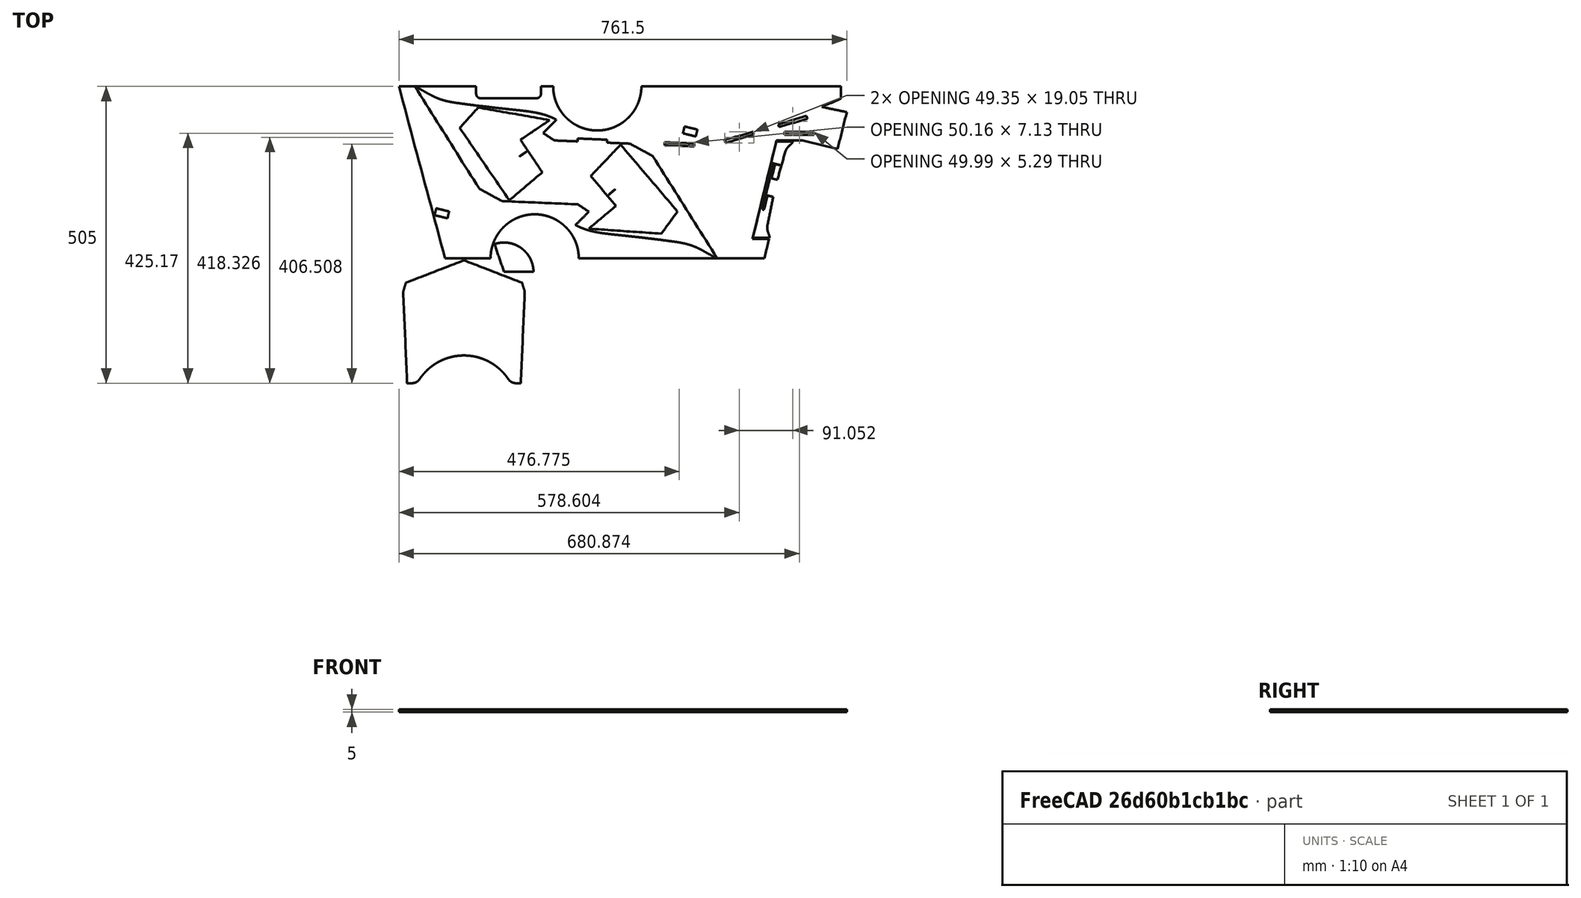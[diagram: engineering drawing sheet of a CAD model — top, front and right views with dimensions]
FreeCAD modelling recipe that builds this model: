
FCSTD DOCUMENT  (FreeCAD 0.19R)
Label: F-35 Page 2
License: All rights reserved
LicenseURL: http://en.wikipedia.org/wiki/All_rights_reserved
objects: Sketcher::SketchObject×7, PartDesign::Pad×7, PartDesign::Body×7
note: 28 computed .brp shape members not serialized (recipe doc carries the construction recipe); baked Part::Feature solids carry a one-line shape summary decoded from their .brp

FEATURE [Sketcher::SketchObject] Sketch
  FullyConstrained = false
  sketch-geometry (125):
    g0: BSplineCurve PolesCount=2 KnotsCount=2 Degree=1 IsPeriodic=0
    g1: BSplineCurve PolesCount=2 KnotsCount=2 Degree=1 IsPeriodic=0
    g2: BSplineCurve PolesCount=2 KnotsCount=2 Degree=1 IsPeriodic=0
    g3: BSplineCurve PolesCount=2 KnotsCount=2 Degree=1 IsPeriodic=0
    g4: BSplineCurve PolesCount=2 KnotsCount=2 Degree=1 IsPeriodic=0
    g5: BSplineCurve PolesCount=2 KnotsCount=2 Degree=1 IsPeriodic=0
    g6: BSplineCurve PolesCount=2 KnotsCount=2 Degree=1 IsPeriodic=0
    g7: BSplineCurve PolesCount=2 KnotsCount=2 Degree=1 IsPeriodic=0
    g8: BSplineCurve PolesCount=2 KnotsCount=2 Degree=1 IsPeriodic=0
    g9: BSplineCurve PolesCount=2 KnotsCount=2 Degree=1 IsPeriodic=0
    g10: BSplineCurve PolesCount=2 KnotsCount=2 Degree=1 IsPeriodic=0
    g11: BSplineCurve PolesCount=2 KnotsCount=2 Degree=1 IsPeriodic=0
    g12: BSplineCurve PolesCount=2 KnotsCount=2 Degree=1 IsPeriodic=0
    g13: BSplineCurve PolesCount=2 KnotsCount=2 Degree=1 IsPeriodic=0
    g14: BSplineCurve PolesCount=2 KnotsCount=2 Degree=1 IsPeriodic=0
    g15: BSplineCurve PolesCount=2 KnotsCount=2 Degree=1 IsPeriodic=0
    g16: BSplineCurve PolesCount=2 KnotsCount=2 Degree=1 IsPeriodic=0
    g17: BSplineCurve PolesCount=2 KnotsCount=2 Degree=1 IsPeriodic=0
    g18: BSplineCurve PolesCount=2 KnotsCount=2 Degree=1 IsPeriodic=0
    g19: BSplineCurve PolesCount=2 KnotsCount=2 Degree=1 IsPeriodic=0
    g20: BSplineCurve PolesCount=2 KnotsCount=2 Degree=1 IsPeriodic=0
    g21: BSplineCurve PolesCount=2 KnotsCount=2 Degree=1 IsPeriodic=0
    g22: BSplineCurve PolesCount=2 KnotsCount=2 Degree=1 IsPeriodic=0
    g23: BSplineCurve PolesCount=2 KnotsCount=2 Degree=1 IsPeriodic=0
    g24: BSplineCurve PolesCount=2 KnotsCount=2 Degree=1 IsPeriodic=0
    g25: BSplineCurve PolesCount=2 KnotsCount=2 Degree=1 IsPeriodic=0
    g26: BSplineCurve PolesCount=2 KnotsCount=2 Degree=1 IsPeriodic=0
    g27: BSplineCurve PolesCount=2 KnotsCount=2 Degree=1 IsPeriodic=0
    g28: BSplineCurve PolesCount=2 KnotsCount=2 Degree=1 IsPeriodic=0
    g29: BSplineCurve PolesCount=2 KnotsCount=2 Degree=1 IsPeriodic=0
    g30: BSplineCurve PolesCount=2 KnotsCount=2 Degree=1 IsPeriodic=0
    g31: BSplineCurve PolesCount=2 KnotsCount=2 Degree=1 IsPeriodic=0
    g32: BSplineCurve PolesCount=2 KnotsCount=2 Degree=1 IsPeriodic=0
    g33: BSplineCurve PolesCount=2 KnotsCount=2 Degree=1 IsPeriodic=0
    g34: BSplineCurve PolesCount=2 KnotsCount=2 Degree=1 IsPeriodic=0
    g35: BSplineCurve PolesCount=2 KnotsCount=2 Degree=1 IsPeriodic=0
    g36: BSplineCurve PolesCount=2 KnotsCount=2 Degree=1 IsPeriodic=0
    g37: BSplineCurve PolesCount=2 KnotsCount=2 Degree=1 IsPeriodic=0
    g38: BSplineCurve PolesCount=2 KnotsCount=2 Degree=1 IsPeriodic=0
    g39: BSplineCurve PolesCount=2 KnotsCount=2 Degree=1 IsPeriodic=0
    g40: BSplineCurve PolesCount=2 KnotsCount=2 Degree=1 IsPeriodic=0
    g41: BSplineCurve PolesCount=2 KnotsCount=2 Degree=1 IsPeriodic=0
    g42: BSplineCurve PolesCount=2 KnotsCount=2 Degree=1 IsPeriodic=0
    g43: BSplineCurve PolesCount=2 KnotsCount=2 Degree=1 IsPeriodic=0
    g44: BSplineCurve PolesCount=2 KnotsCount=2 Degree=1 IsPeriodic=0
    g45: BSplineCurve PolesCount=2 KnotsCount=2 Degree=1 IsPeriodic=0
    g46: BSplineCurve PolesCount=2 KnotsCount=2 Degree=1 IsPeriodic=0
    g47: BSplineCurve PolesCount=2 KnotsCount=2 Degree=1 IsPeriodic=0
    g48: BSplineCurve PolesCount=2 KnotsCount=2 Degree=1 IsPeriodic=0
    g49: BSplineCurve PolesCount=2 KnotsCount=2 Degree=1 IsPeriodic=0
    g50: BSplineCurve PolesCount=2 KnotsCount=2 Degree=1 IsPeriodic=0
    g51: BSplineCurve PolesCount=2 KnotsCount=2 Degree=1 IsPeriodic=0
    g52: BSplineCurve PolesCount=2 KnotsCount=2 Degree=1 IsPeriodic=0
    g53: BSplineCurve PolesCount=2 KnotsCount=2 Degree=1 IsPeriodic=0
    g54: BSplineCurve PolesCount=2 KnotsCount=2 Degree=1 IsPeriodic=0
    g55: BSplineCurve PolesCount=2 KnotsCount=2 Degree=1 IsPeriodic=0
    g56: BSplineCurve PolesCount=2 KnotsCount=2 Degree=1 IsPeriodic=0
    g57: BSplineCurve PolesCount=2 KnotsCount=2 Degree=1 IsPeriodic=0
    g58: BSplineCurve PolesCount=2 KnotsCount=2 Degree=1 IsPeriodic=0
    g59: BSplineCurve PolesCount=2 KnotsCount=2 Degree=1 IsPeriodic=0
    g60: BSplineCurve PolesCount=2 KnotsCount=2 Degree=1 IsPeriodic=0
    g61: BSplineCurve PolesCount=2 KnotsCount=2 Degree=1 IsPeriodic=0
    g62: BSplineCurve PolesCount=2 KnotsCount=2 Degree=1 IsPeriodic=0
    g63: BSplineCurve PolesCount=2 KnotsCount=2 Degree=1 IsPeriodic=0
    g64: BSplineCurve PolesCount=2 KnotsCount=2 Degree=1 IsPeriodic=0
    g65: BSplineCurve PolesCount=2 KnotsCount=2 Degree=1 IsPeriodic=0
    g66: BSplineCurve PolesCount=2 KnotsCount=2 Degree=1 IsPeriodic=0
    g67: BSplineCurve PolesCount=2 KnotsCount=2 Degree=1 IsPeriodic=0
    g68: BSplineCurve PolesCount=2 KnotsCount=2 Degree=1 IsPeriodic=0
    g69: BSplineCurve PolesCount=2 KnotsCount=2 Degree=1 IsPeriodic=0
    g70: BSplineCurve PolesCount=2 KnotsCount=2 Degree=1 IsPeriodic=0
    g71: BSplineCurve PolesCount=2 KnotsCount=2 Degree=1 IsPeriodic=0
    g72: BSplineCurve PolesCount=2 KnotsCount=2 Degree=1 IsPeriodic=0
    g73: BSplineCurve PolesCount=2 KnotsCount=2 Degree=1 IsPeriodic=0
    g74: BSplineCurve PolesCount=2 KnotsCount=2 Degree=1 IsPeriodic=0
    g75: BSplineCurve PolesCount=2 KnotsCount=2 Degree=1 IsPeriodic=0
    g76: BSplineCurve PolesCount=2 KnotsCount=2 Degree=1 IsPeriodic=0
    g77: BSplineCurve PolesCount=2 KnotsCount=2 Degree=1 IsPeriodic=0
    g78: BSplineCurve PolesCount=2 KnotsCount=2 Degree=1 IsPeriodic=0
    g79: BSplineCurve PolesCount=2 KnotsCount=2 Degree=1 IsPeriodic=0
    g80: BSplineCurve PolesCount=2 KnotsCount=2 Degree=1 IsPeriodic=0
    g81: BSplineCurve PolesCount=2 KnotsCount=2 Degree=1 IsPeriodic=0
    g82: BSplineCurve PolesCount=2 KnotsCount=2 Degree=1 IsPeriodic=0
    g83: BSplineCurve PolesCount=2 KnotsCount=2 Degree=1 IsPeriodic=0
    g84: BSplineCurve PolesCount=2 KnotsCount=2 Degree=1 IsPeriodic=0
    g85: BSplineCurve PolesCount=2 KnotsCount=2 Degree=1 IsPeriodic=0
    g86: BSplineCurve PolesCount=2 KnotsCount=2 Degree=1 IsPeriodic=0
    g87: BSplineCurve PolesCount=2 KnotsCount=2 Degree=1 IsPeriodic=0
    g88: BSplineCurve PolesCount=2 KnotsCount=2 Degree=1 IsPeriodic=0
    g89: BSplineCurve PolesCount=2 KnotsCount=2 Degree=1 IsPeriodic=0
    g90: BSplineCurve PolesCount=2 KnotsCount=2 Degree=1 IsPeriodic=0
    g91: BSplineCurve PolesCount=2 KnotsCount=2 Degree=1 IsPeriodic=0
    g92: BSplineCurve PolesCount=2 KnotsCount=2 Degree=1 IsPeriodic=0
    g93: BSplineCurve PolesCount=2 KnotsCount=2 Degree=1 IsPeriodic=0
    g94: BSplineCurve PolesCount=2 KnotsCount=2 Degree=1 IsPeriodic=0
    g95: BSplineCurve PolesCount=2 KnotsCount=2 Degree=1 IsPeriodic=0
    g96: BSplineCurve PolesCount=2 KnotsCount=2 Degree=1 IsPeriodic=0
    g97: BSplineCurve PolesCount=2 KnotsCount=2 Degree=1 IsPeriodic=0
    g98: BSplineCurve PolesCount=2 KnotsCount=2 Degree=1 IsPeriodic=0
    g99: BSplineCurve PolesCount=2 KnotsCount=2 Degree=1 IsPeriodic=0
    g100: BSplineCurve PolesCount=2 KnotsCount=2 Degree=1 IsPeriodic=0
    g101: BSplineCurve PolesCount=2 KnotsCount=2 Degree=1 IsPeriodic=0
    g102: BSplineCurve PolesCount=2 KnotsCount=2 Degree=1 IsPeriodic=0
    g103: BSplineCurve PolesCount=2 KnotsCount=2 Degree=1 IsPeriodic=0
    g104: BSplineCurve PolesCount=2 KnotsCount=2 Degree=1 IsPeriodic=0
    g105: BSplineCurve PolesCount=2 KnotsCount=2 Degree=1 IsPeriodic=0
    g106: BSplineCurve PolesCount=2 KnotsCount=2 Degree=1 IsPeriodic=0
    g107: BSplineCurve PolesCount=2 KnotsCount=2 Degree=1 IsPeriodic=0
    g108: BSplineCurve PolesCount=2 KnotsCount=2 Degree=1 IsPeriodic=0
    g109: BSplineCurve PolesCount=2 KnotsCount=2 Degree=1 IsPeriodic=0
    g110: BSplineCurve PolesCount=2 KnotsCount=2 Degree=1 IsPeriodic=0
    g111: BSplineCurve PolesCount=2 KnotsCount=2 Degree=1 IsPeriodic=0
    g112: BSplineCurve PolesCount=2 KnotsCount=2 Degree=1 IsPeriodic=0
    g113: BSplineCurve PolesCount=2 KnotsCount=2 Degree=1 IsPeriodic=0
    g114: BSplineCurve PolesCount=2 KnotsCount=2 Degree=1 IsPeriodic=0
    g115: BSplineCurve PolesCount=2 KnotsCount=2 Degree=1 IsPeriodic=0
    g116: BSplineCurve PolesCount=2 KnotsCount=2 Degree=1 IsPeriodic=0
    g117: BSplineCurve PolesCount=2 KnotsCount=2 Degree=1 IsPeriodic=0
    g118: BSplineCurve PolesCount=2 KnotsCount=2 Degree=1 IsPeriodic=0
    g119: BSplineCurve PolesCount=2 KnotsCount=2 Degree=1 IsPeriodic=0
    g120: BSplineCurve PolesCount=2 KnotsCount=2 Degree=1 IsPeriodic=0
    g121: BSplineCurve PolesCount=2 KnotsCount=2 Degree=1 IsPeriodic=0
    g122: BSplineCurve PolesCount=2 KnotsCount=2 Degree=1 IsPeriodic=0
    g123: BSplineCurve PolesCount=2 KnotsCount=2 Degree=1 IsPeriodic=0
    g124: BSplineCurve PolesCount=2 KnotsCount=2 Degree=1 IsPeriodic=0
  constraints (76):
    c: Coincident(g20,g21)
    c: Coincident(g21,g22)
    c: Coincident(g22,g23)
    c: Coincident(g23,g24)
    c: Coincident(g24,g25)
    c: Coincident(g25,g26)
    c: Coincident(g26,g27)
    c: Coincident(g29,g30)
    c: Coincident(g30,g31)
    c: Coincident(g31,g32)
    c: Coincident(g32,g33)
    c: Coincident(g33,g34)
    c: Coincident(g34,g35)
    c: Coincident(g35,g36)
    c: Coincident(g39,g40)
    c: Coincident(g40,g41)
    c: Coincident(g41,g42)
    c: Coincident(g42,g43)
    c: Coincident(g43,g44)
    c: Coincident(g44,g45)
    c: Coincident(g45,g46)
    c: Coincident(g46,g47)
    c: Coincident(g47,g48)
    c: Coincident(g48,g49)
    c: Coincident(g49,g50)
    c: Coincident(g50,g51)
    c: Coincident(g51,g52)
    c: Coincident(g52,g53)
    c: Coincident(g53,g54)
    c: Coincident(g54,g55)
    c: Coincident(g55,g56)
    c: Coincident(g56,g57)
    c: Coincident(g57,g58)
    c: Coincident(g58,g59)
    c: Coincident(g59,g60)
    c: Coincident(g60,g61)
    c: Coincident(g61,g62)
    c: Coincident(g62,g63)
    c: Coincident(g63,g64)
    c: Coincident(g64,g65)
    c: Coincident(g65,g66)
    c: Coincident(g66,g67)
    c: Coincident(g67,g68)
    c: Coincident(g68,g69)
    c: Coincident(g69,g70)
    c: Coincident(g70,g71)
    c: Coincident(g71,g72)
    c: Coincident(g72,g73)
    c: Coincident(g73,g74)
    c: Coincident(g74,g75)
    c: Coincident(g75,g76)
    c: Coincident(g76,g77)
    c: Coincident(g77,g78)
    c: Coincident(g78,g79)
    c: Coincident(g79,g80)
    c: Coincident(g80,g81)
    c: Coincident(g81,g82)
    c: Coincident(g82,g83)
    c: Coincident(g103,g104)
    c: Coincident(g104,g105)
    c: Coincident(g105,g106)
    c: Coincident(g106,g107)
    c: Coincident(g107,g108)
    c: Coincident(g108,g109)
    c: Coincident(g109,g110)
    c: Coincident(g110,g111)
    c: Coincident(g111,g112)
    c: Coincident(g112,g113)
    c: Coincident(g113,g114)
    c: Coincident(g114,g115)
    c: Coincident(g115,g116)
    c: Coincident(g116,g117)
    c: Coincident(g117,g118)
    c: Coincident(g118,g119)
    c: Coincident(g119,g120)
    c: Coincident(g120,g121)
FEATURE [Sketcher::SketchObject] Sketch001
  FullyConstrained = false
  sketch-geometry (36):
    g0: BSplineCurve PolesCount=2 KnotsCount=2 Degree=1 IsPeriodic=0
    g1: BSplineCurve PolesCount=2 KnotsCount=2 Degree=1 IsPeriodic=0
    g2: BSplineCurve PolesCount=2 KnotsCount=2 Degree=1 IsPeriodic=0
    g3: BSplineCurve PolesCount=2 KnotsCount=2 Degree=1 IsPeriodic=0
    g4: BSplineCurve PolesCount=2 KnotsCount=2 Degree=1 IsPeriodic=0
    g5: BSplineCurve PolesCount=2 KnotsCount=2 Degree=1 IsPeriodic=0
    g6: BSplineCurve PolesCount=2 KnotsCount=2 Degree=1 IsPeriodic=0
    g7: BSplineCurve PolesCount=2 KnotsCount=2 Degree=1 IsPeriodic=0
    g8: BSplineCurve PolesCount=2 KnotsCount=2 Degree=1 IsPeriodic=0
    g9: BSplineCurve PolesCount=2 KnotsCount=2 Degree=1 IsPeriodic=0
    g10: BSplineCurve PolesCount=2 KnotsCount=2 Degree=1 IsPeriodic=0
    g11: BSplineCurve PolesCount=2 KnotsCount=2 Degree=1 IsPeriodic=0
    g12: BSplineCurve PolesCount=2 KnotsCount=2 Degree=1 IsPeriodic=0
    g13: BSplineCurve PolesCount=2 KnotsCount=2 Degree=1 IsPeriodic=0
    g14: BSplineCurve PolesCount=2 KnotsCount=2 Degree=1 IsPeriodic=0
    g15: BSplineCurve PolesCount=2 KnotsCount=2 Degree=1 IsPeriodic=0
    g16: BSplineCurve PolesCount=2 KnotsCount=2 Degree=1 IsPeriodic=0
    g17: BSplineCurve PolesCount=2 KnotsCount=2 Degree=1 IsPeriodic=0
    g18: BSplineCurve PolesCount=2 KnotsCount=2 Degree=1 IsPeriodic=0
    g19: BSplineCurve PolesCount=2 KnotsCount=2 Degree=1 IsPeriodic=0
    g20: BSplineCurve PolesCount=2 KnotsCount=2 Degree=1 IsPeriodic=0
    g21: BSplineCurve PolesCount=2 KnotsCount=2 Degree=1 IsPeriodic=0
    g22: BSplineCurve PolesCount=2 KnotsCount=2 Degree=1 IsPeriodic=0
    g23: BSplineCurve PolesCount=2 KnotsCount=2 Degree=1 IsPeriodic=0
    g24: BSplineCurve PolesCount=2 KnotsCount=2 Degree=1 IsPeriodic=0
    g25: BSplineCurve PolesCount=2 KnotsCount=2 Degree=1 IsPeriodic=0
    g26: BSplineCurve PolesCount=2 KnotsCount=2 Degree=1 IsPeriodic=0
    g27: BSplineCurve PolesCount=2 KnotsCount=2 Degree=1 IsPeriodic=0
    g28: BSplineCurve PolesCount=2 KnotsCount=2 Degree=1 IsPeriodic=0
    g29: BSplineCurve PolesCount=2 KnotsCount=2 Degree=1 IsPeriodic=0
    g30: BSplineCurve PolesCount=2 KnotsCount=2 Degree=1 IsPeriodic=0
    g31: BSplineCurve PolesCount=2 KnotsCount=2 Degree=1 IsPeriodic=0
    g32: BSplineCurve PolesCount=2 KnotsCount=2 Degree=1 IsPeriodic=0
    g33: BSplineCurve PolesCount=2 KnotsCount=2 Degree=1 IsPeriodic=0
    g34: BSplineCurve PolesCount=2 KnotsCount=2 Degree=1 IsPeriodic=0
    g35: LineSegment StartX=748.511 StartY=-199.265 StartZ=0 EndX=708.789 EndY=-363.131 EndZ=0
  constraints (16):
    c: Coincident(g11,g12)
    c: Coincident(g12,g13)
    c: Coincident(g13,g14)
    c: Coincident(g14,g15)
    c: Coincident(g15,g16)
    c: Coincident(g16,g17)
    c: Coincident(g17,g18)
    c: Coincident(g27,g28)
    c: Coincident(g28,g29)
    c: Coincident(g29,g30)
    c: Coincident(g30,g31)
    c: Coincident(g31,g32)
    c: Coincident(g32,g33)
    c: Coincident(g33,g34)
    c: Coincident(g7,g35)
    c: Coincident(g8,g35)
FEATURE [Sketcher::SketchObject] Sketch002
  FullyConstrained = false
  sketch-geometry (77):
    g0: BSplineCurve PolesCount=2 KnotsCount=2 Degree=1 IsPeriodic=0
    g1: BSplineCurve PolesCount=2 KnotsCount=2 Degree=1 IsPeriodic=0
    g2: BSplineCurve PolesCount=2 KnotsCount=2 Degree=1 IsPeriodic=0
    g3: BSplineCurve PolesCount=2 KnotsCount=2 Degree=1 IsPeriodic=0
    g4: BSplineCurve PolesCount=2 KnotsCount=2 Degree=1 IsPeriodic=0
    g5: BSplineCurve PolesCount=2 KnotsCount=2 Degree=1 IsPeriodic=0
    g6: BSplineCurve PolesCount=2 KnotsCount=2 Degree=1 IsPeriodic=0
    g7: BSplineCurve PolesCount=2 KnotsCount=2 Degree=1 IsPeriodic=0
    g8: BSplineCurve PolesCount=2 KnotsCount=2 Degree=1 IsPeriodic=0
    g9: BSplineCurve PolesCount=2 KnotsCount=2 Degree=1 IsPeriodic=0
    g10: BSplineCurve PolesCount=2 KnotsCount=2 Degree=1 IsPeriodic=0
    g11: BSplineCurve PolesCount=2 KnotsCount=2 Degree=1 IsPeriodic=0
    g12: BSplineCurve PolesCount=2 KnotsCount=2 Degree=1 IsPeriodic=0
    g13: BSplineCurve PolesCount=2 KnotsCount=2 Degree=1 IsPeriodic=0
    g14: BSplineCurve PolesCount=2 KnotsCount=2 Degree=1 IsPeriodic=0
    g15: BSplineCurve PolesCount=2 KnotsCount=2 Degree=1 IsPeriodic=0
    g16: BSplineCurve PolesCount=2 KnotsCount=2 Degree=1 IsPeriodic=0
    g17: BSplineCurve PolesCount=2 KnotsCount=2 Degree=1 IsPeriodic=0
    g18: BSplineCurve PolesCount=2 KnotsCount=2 Degree=1 IsPeriodic=0
    g19: BSplineCurve PolesCount=2 KnotsCount=2 Degree=1 IsPeriodic=0
    g20: BSplineCurve PolesCount=2 KnotsCount=2 Degree=1 IsPeriodic=0
    g21: BSplineCurve PolesCount=2 KnotsCount=2 Degree=1 IsPeriodic=0
    g22: BSplineCurve PolesCount=2 KnotsCount=2 Degree=1 IsPeriodic=0
    g23: BSplineCurve PolesCount=2 KnotsCount=2 Degree=1 IsPeriodic=0
    g24: BSplineCurve PolesCount=2 KnotsCount=2 Degree=1 IsPeriodic=0
    g25: BSplineCurve PolesCount=2 KnotsCount=2 Degree=1 IsPeriodic=0
    g26: BSplineCurve PolesCount=2 KnotsCount=2 Degree=1 IsPeriodic=0
    g27: BSplineCurve PolesCount=2 KnotsCount=2 Degree=1 IsPeriodic=0
    g28: BSplineCurve PolesCount=2 KnotsCount=2 Degree=1 IsPeriodic=0
    g29: BSplineCurve PolesCount=2 KnotsCount=2 Degree=1 IsPeriodic=0
    g30: BSplineCurve PolesCount=2 KnotsCount=2 Degree=1 IsPeriodic=0
    g31: BSplineCurve PolesCount=2 KnotsCount=2 Degree=1 IsPeriodic=0
    g32: BSplineCurve PolesCount=2 KnotsCount=2 Degree=1 IsPeriodic=0
    g33: BSplineCurve PolesCount=2 KnotsCount=2 Degree=1 IsPeriodic=0
    g34: BSplineCurve PolesCount=2 KnotsCount=2 Degree=1 IsPeriodic=0
    g35: BSplineCurve PolesCount=2 KnotsCount=2 Degree=1 IsPeriodic=0
    g36: BSplineCurve PolesCount=2 KnotsCount=2 Degree=1 IsPeriodic=0
    g37: BSplineCurve PolesCount=2 KnotsCount=2 Degree=1 IsPeriodic=0
    g38: BSplineCurve PolesCount=2 KnotsCount=2 Degree=1 IsPeriodic=0
    g39: BSplineCurve PolesCount=2 KnotsCount=2 Degree=1 IsPeriodic=0
    g40: BSplineCurve PolesCount=2 KnotsCount=2 Degree=1 IsPeriodic=0
    g41: BSplineCurve PolesCount=2 KnotsCount=2 Degree=1 IsPeriodic=0
    g42: BSplineCurve PolesCount=2 KnotsCount=2 Degree=1 IsPeriodic=0
    g43: BSplineCurve PolesCount=2 KnotsCount=2 Degree=1 IsPeriodic=0
    g44: BSplineCurve PolesCount=2 KnotsCount=2 Degree=1 IsPeriodic=0
    g45: BSplineCurve PolesCount=2 KnotsCount=2 Degree=1 IsPeriodic=0
    g46: BSplineCurve PolesCount=2 KnotsCount=2 Degree=1 IsPeriodic=0
    g47: BSplineCurve PolesCount=2 KnotsCount=2 Degree=1 IsPeriodic=0
    g48: BSplineCurve PolesCount=2 KnotsCount=2 Degree=1 IsPeriodic=0
    g49: BSplineCurve PolesCount=2 KnotsCount=2 Degree=1 IsPeriodic=0
    g50: BSplineCurve PolesCount=2 KnotsCount=2 Degree=1 IsPeriodic=0
    g51: BSplineCurve PolesCount=2 KnotsCount=2 Degree=1 IsPeriodic=0
    g52: BSplineCurve PolesCount=2 KnotsCount=2 Degree=1 IsPeriodic=0
    g53: BSplineCurve PolesCount=2 KnotsCount=2 Degree=1 IsPeriodic=0
    g54: BSplineCurve PolesCount=2 KnotsCount=2 Degree=1 IsPeriodic=0
    g55: BSplineCurve PolesCount=2 KnotsCount=2 Degree=1 IsPeriodic=0
    g56: BSplineCurve PolesCount=2 KnotsCount=2 Degree=1 IsPeriodic=0
    g57: BSplineCurve PolesCount=2 KnotsCount=2 Degree=1 IsPeriodic=0
    g58: BSplineCurve PolesCount=2 KnotsCount=2 Degree=1 IsPeriodic=0
    g59: BSplineCurve PolesCount=2 KnotsCount=2 Degree=1 IsPeriodic=0
    g60: BSplineCurve PolesCount=2 KnotsCount=2 Degree=1 IsPeriodic=0
    g61: BSplineCurve PolesCount=2 KnotsCount=2 Degree=1 IsPeriodic=0
    g62: BSplineCurve PolesCount=2 KnotsCount=2 Degree=1 IsPeriodic=0
    g63: BSplineCurve PolesCount=2 KnotsCount=2 Degree=1 IsPeriodic=0
    g64: BSplineCurve PolesCount=2 KnotsCount=2 Degree=1 IsPeriodic=0
    g65: BSplineCurve PolesCount=2 KnotsCount=2 Degree=1 IsPeriodic=0
    g66: BSplineCurve PolesCount=2 KnotsCount=2 Degree=1 IsPeriodic=0
    g67: BSplineCurve PolesCount=2 KnotsCount=2 Degree=1 IsPeriodic=0
    g68: BSplineCurve PolesCount=2 KnotsCount=2 Degree=1 IsPeriodic=0
    g69: BSplineCurve PolesCount=2 KnotsCount=2 Degree=1 IsPeriodic=0
    g70: BSplineCurve PolesCount=2 KnotsCount=2 Degree=1 IsPeriodic=0
    g71: BSplineCurve PolesCount=2 KnotsCount=2 Degree=1 IsPeriodic=0
    g72: BSplineCurve PolesCount=2 KnotsCount=2 Degree=1 IsPeriodic=0
    g73: BSplineCurve PolesCount=2 KnotsCount=2 Degree=1 IsPeriodic=0
    g74: BSplineCurve PolesCount=2 KnotsCount=2 Degree=1 IsPeriodic=0
    g75: BSplineCurve PolesCount=2 KnotsCount=2 Degree=1 IsPeriodic=0
    g76: BSplineCurve PolesCount=2 KnotsCount=2 Degree=1 IsPeriodic=0
  constraints (62):
    c: Coincident(g6,g7)
    c: Coincident(g7,g8)
    c: Coincident(g8,g9)
    c: Coincident(g9,g10)
    c: Coincident(g10,g11)
    c: Coincident(g11,g12)
    c: Coincident(g12,g13)
    c: Coincident(g13,g14)
    c: Coincident(g14,g15)
    c: Coincident(g15,g16)
    c: Coincident(g16,g17)
    c: Coincident(g17,g18)
    c: Coincident(g18,g19)
    c: Coincident(g19,g20)
    c: Coincident(g20,g21)
    c: Coincident(g21,g22)
    c: Coincident(g22,g23)
    c: Coincident(g23,g24)
    c: Coincident(g25,g26)
    c: Coincident(g26,g27)
    c: Coincident(g27,g28)
    c: Coincident(g28,g29)
    c: Coincident(g29,g30)
    c: Coincident(g30,g31)
    c: Coincident(g31,g32)
    c: Coincident(g32,g33)
    c: Coincident(g33,g34)
    c: Coincident(g34,g35)
    c: Coincident(g35,g36)
    c: Coincident(g36,g37)
    c: Coincident(g37,g38)
    c: Coincident(g38,g39)
    c: Coincident(g39,g40)
    c: Coincident(g40,g41)
    c: Coincident(g41,g42)
    c: Coincident(g42,g43)
    c: Coincident(g43,g44)
    c: Coincident(g44,g45)
    c: Coincident(g45,g46)
    c: Coincident(g46,g47)
    c: Coincident(g47,g48)
    c: Coincident(g48,g49)
    c: Coincident(g49,g50)
    c: Coincident(g50,g51)
    c: Coincident(g51,g52)
    c: Coincident(g52,g53)
    c: Coincident(g53,g54)
    c: Coincident(g54,g55)
    c: Coincident(g55,g56)
    c: Coincident(g56,g57)
    c: Coincident(g57,g58)
    c: Coincident(g58,g59)
    c: Coincident(g59,g60)
    c: Coincident(g60,g61)
    c: Coincident(g61,g62)
    c: Coincident(g62,g63)
    c: Coincident(g63,g64)
    c: Coincident(g64,g65)
    c: Coincident(g65,g66)
    c: Coincident(g66,g67)
    c: Coincident(g67,g68)
    c: Coincident(g68,g69)
FEATURE [Sketcher::SketchObject] Sketch003
  FullyConstrained = false
  sketch-geometry (10):
    g0: BSplineCurve PolesCount=2 KnotsCount=2 Degree=1 IsPeriodic=0
    g1: BSplineCurve PolesCount=2 KnotsCount=2 Degree=1 IsPeriodic=0
    g2: BSplineCurve PolesCount=2 KnotsCount=2 Degree=1 IsPeriodic=0
    g3: BSplineCurve PolesCount=2 KnotsCount=2 Degree=1 IsPeriodic=0
    g4: BSplineCurve PolesCount=2 KnotsCount=2 Degree=1 IsPeriodic=0
    g5: BSplineCurve PolesCount=2 KnotsCount=2 Degree=1 IsPeriodic=0
    g6: BSplineCurve PolesCount=2 KnotsCount=2 Degree=1 IsPeriodic=0
    g7: BSplineCurve PolesCount=2 KnotsCount=2 Degree=1 IsPeriodic=0
    g8: BSplineCurve PolesCount=2 KnotsCount=2 Degree=1 IsPeriodic=0
    g9: BSplineCurve PolesCount=2 KnotsCount=2 Degree=1 IsPeriodic=0
FEATURE [Sketcher::SketchObject] Sketch004
  FullyConstrained = false
  sketch-geometry (10):
    g0: BSplineCurve PolesCount=2 KnotsCount=2 Degree=1 IsPeriodic=0
    g1: BSplineCurve PolesCount=2 KnotsCount=2 Degree=1 IsPeriodic=0
    g2: BSplineCurve PolesCount=2 KnotsCount=2 Degree=1 IsPeriodic=0
    g3: BSplineCurve PolesCount=2 KnotsCount=2 Degree=1 IsPeriodic=0
    g4: BSplineCurve PolesCount=2 KnotsCount=2 Degree=1 IsPeriodic=0
    g5: BSplineCurve PolesCount=2 KnotsCount=2 Degree=1 IsPeriodic=0
    g6: BSplineCurve PolesCount=2 KnotsCount=2 Degree=1 IsPeriodic=0
    g7: BSplineCurve PolesCount=2 KnotsCount=2 Degree=1 IsPeriodic=0
    g8: BSplineCurve PolesCount=2 KnotsCount=2 Degree=1 IsPeriodic=0
    g9: BSplineCurve PolesCount=2 KnotsCount=2 Degree=1 IsPeriodic=0
FEATURE [Sketcher::SketchObject] Sketch005
  FullyConstrained = false
  sketch-geometry (65):
    g0: BSplineCurve PolesCount=2 KnotsCount=2 Degree=1 IsPeriodic=0
    g1: BSplineCurve PolesCount=2 KnotsCount=2 Degree=1 IsPeriodic=0
    g2: BSplineCurve PolesCount=2 KnotsCount=2 Degree=1 IsPeriodic=0
    g3: BSplineCurve PolesCount=2 KnotsCount=2 Degree=1 IsPeriodic=0
    g4: BSplineCurve PolesCount=2 KnotsCount=2 Degree=1 IsPeriodic=0
    g5: BSplineCurve PolesCount=2 KnotsCount=2 Degree=1 IsPeriodic=0
    g6: BSplineCurve PolesCount=2 KnotsCount=2 Degree=1 IsPeriodic=0
    g7: BSplineCurve PolesCount=2 KnotsCount=2 Degree=1 IsPeriodic=0
    g8: BSplineCurve PolesCount=2 KnotsCount=2 Degree=1 IsPeriodic=0
    g9: BSplineCurve PolesCount=2 KnotsCount=2 Degree=1 IsPeriodic=0
    g10: BSplineCurve PolesCount=2 KnotsCount=2 Degree=1 IsPeriodic=0
    g11: BSplineCurve PolesCount=2 KnotsCount=2 Degree=1 IsPeriodic=0
    g12: BSplineCurve PolesCount=2 KnotsCount=2 Degree=1 IsPeriodic=0
    g13: BSplineCurve PolesCount=2 KnotsCount=2 Degree=1 IsPeriodic=0
    g14: BSplineCurve PolesCount=2 KnotsCount=2 Degree=1 IsPeriodic=0
    g15: BSplineCurve PolesCount=2 KnotsCount=2 Degree=1 IsPeriodic=0
    g16: BSplineCurve PolesCount=2 KnotsCount=2 Degree=1 IsPeriodic=0
    g17: BSplineCurve PolesCount=2 KnotsCount=2 Degree=1 IsPeriodic=0
    g18: BSplineCurve PolesCount=2 KnotsCount=2 Degree=1 IsPeriodic=0
    g19: BSplineCurve PolesCount=2 KnotsCount=2 Degree=1 IsPeriodic=0
    g20: BSplineCurve PolesCount=2 KnotsCount=2 Degree=1 IsPeriodic=0
    g21: BSplineCurve PolesCount=2 KnotsCount=2 Degree=1 IsPeriodic=0
    g22: BSplineCurve PolesCount=2 KnotsCount=2 Degree=1 IsPeriodic=0
    g23: BSplineCurve PolesCount=2 KnotsCount=2 Degree=1 IsPeriodic=0
    g24: BSplineCurve PolesCount=2 KnotsCount=2 Degree=1 IsPeriodic=0
    g25: BSplineCurve PolesCount=2 KnotsCount=2 Degree=1 IsPeriodic=0
    g26: BSplineCurve PolesCount=2 KnotsCount=2 Degree=1 IsPeriodic=0
    g27: BSplineCurve PolesCount=2 KnotsCount=2 Degree=1 IsPeriodic=0
    g28: BSplineCurve PolesCount=2 KnotsCount=2 Degree=1 IsPeriodic=0
    g29: BSplineCurve PolesCount=2 KnotsCount=2 Degree=1 IsPeriodic=0
    g30: BSplineCurve PolesCount=2 KnotsCount=2 Degree=1 IsPeriodic=0
    g31: BSplineCurve PolesCount=2 KnotsCount=2 Degree=1 IsPeriodic=0
    g32: BSplineCurve PolesCount=2 KnotsCount=2 Degree=1 IsPeriodic=0
    g33: BSplineCurve PolesCount=2 KnotsCount=2 Degree=1 IsPeriodic=0
    g34: BSplineCurve PolesCount=2 KnotsCount=2 Degree=1 IsPeriodic=0
    g35: BSplineCurve PolesCount=2 KnotsCount=2 Degree=1 IsPeriodic=0
    g36: BSplineCurve PolesCount=2 KnotsCount=2 Degree=1 IsPeriodic=0
    g37: BSplineCurve PolesCount=2 KnotsCount=2 Degree=1 IsPeriodic=0
    g38: BSplineCurve PolesCount=2 KnotsCount=2 Degree=1 IsPeriodic=0
    g39: BSplineCurve PolesCount=2 KnotsCount=2 Degree=1 IsPeriodic=0
    g40: BSplineCurve PolesCount=2 KnotsCount=2 Degree=1 IsPeriodic=0
    g41: BSplineCurve PolesCount=2 KnotsCount=2 Degree=1 IsPeriodic=0
    g42: BSplineCurve PolesCount=2 KnotsCount=2 Degree=1 IsPeriodic=0
    g43: BSplineCurve PolesCount=2 KnotsCount=2 Degree=1 IsPeriodic=0
    g44: BSplineCurve PolesCount=2 KnotsCount=2 Degree=1 IsPeriodic=0
    g45: BSplineCurve PolesCount=2 KnotsCount=2 Degree=1 IsPeriodic=0
    g46: BSplineCurve PolesCount=2 KnotsCount=2 Degree=1 IsPeriodic=0
    g47: BSplineCurve PolesCount=2 KnotsCount=2 Degree=1 IsPeriodic=0
    g48: BSplineCurve PolesCount=2 KnotsCount=2 Degree=1 IsPeriodic=0
    g49: BSplineCurve PolesCount=2 KnotsCount=2 Degree=1 IsPeriodic=0
    g50: BSplineCurve PolesCount=2 KnotsCount=2 Degree=1 IsPeriodic=0
    g51: BSplineCurve PolesCount=2 KnotsCount=2 Degree=1 IsPeriodic=0
    g52: BSplineCurve PolesCount=2 KnotsCount=2 Degree=1 IsPeriodic=0
    g53: BSplineCurve PolesCount=2 KnotsCount=2 Degree=1 IsPeriodic=0
    g54: BSplineCurve PolesCount=2 KnotsCount=2 Degree=1 IsPeriodic=0
    g55: BSplineCurve PolesCount=2 KnotsCount=2 Degree=1 IsPeriodic=0
    g56: BSplineCurve PolesCount=2 KnotsCount=2 Degree=1 IsPeriodic=0
    g57: BSplineCurve PolesCount=2 KnotsCount=2 Degree=1 IsPeriodic=0
    g58: BSplineCurve PolesCount=2 KnotsCount=2 Degree=1 IsPeriodic=0
    g59: BSplineCurve PolesCount=2 KnotsCount=2 Degree=1 IsPeriodic=0
    g60: BSplineCurve PolesCount=2 KnotsCount=2 Degree=1 IsPeriodic=0
    g61: BSplineCurve PolesCount=2 KnotsCount=2 Degree=1 IsPeriodic=0
    g62: BSplineCurve PolesCount=2 KnotsCount=2 Degree=1 IsPeriodic=0
    g63: BSplineCurve PolesCount=2 KnotsCount=2 Degree=1 IsPeriodic=0
    g64: BSplineCurve PolesCount=2 KnotsCount=2 Degree=1 IsPeriodic=0
  constraints (54):
    c: Coincident(g0,g1)
    c: Coincident(g1,g2)
    c: Coincident(g2,g3)
    c: Coincident(g3,g4)
    c: Coincident(g4,g5)
    c: Coincident(g5,g6)
    c: Coincident(g6,g7)
    c: Coincident(g9,g10)
    c: Coincident(g10,g11)
    c: Coincident(g11,g12)
    c: Coincident(g12,g13)
    c: Coincident(g13,g14)
    c: Coincident(g14,g15)
    c: Coincident(g15,g16)
    c: Coincident(g16,g17)
    c: Coincident(g17,g18)
    c: Coincident(g18,g19)
    c: Coincident(g19,g20)
    c: Coincident(g20,g21)
    c: Coincident(g21,g22)
    c: Coincident(g22,g23)
    c: Coincident(g23,g24)
    c: Coincident(g24,g25)
    c: Coincident(g25,g26)
    c: Coincident(g26,g27)
    c: Coincident(g27,g28)
    c: Coincident(g28,g29)
    c: Coincident(g29,g30)
    c: Coincident(g30,g31)
    c: Coincident(g31,g32)
    c: Coincident(g32,g33)
    c: Coincident(g33,g34)
    c: Coincident(g34,g35)
    c: Coincident(g35,g36)
    c: Coincident(g36,g37)
    c: Coincident(g37,g38)
    c: Coincident(g38,g39)
    c: Coincident(g39,g40)
    c: Coincident(g40,g41)
    c: Coincident(g41,g42)
    c: Coincident(g42,g43)
    c: Coincident(g43,g44)
    c: Coincident(g44,g45)
    c: Coincident(g45,g46)
    c: Coincident(g46,g47)
    c: Coincident(g47,g48)
    c: Coincident(g48,g49)
    c: Coincident(g51,g52)
    c: Coincident(g52,g53)
    c: Coincident(g53,g54)
    c: Coincident(g54,g55)
    c: Coincident(g55,g56)
    c: Coincident(g56,g57)
    c: Coincident(g57,g58)
FEATURE [Sketcher::SketchObject] Sketch006
  FullyConstrained = false
  sketch-geometry (58):
    g0: BSplineCurve PolesCount=2 KnotsCount=2 Degree=1 IsPeriodic=0
    g1: BSplineCurve PolesCount=2 KnotsCount=2 Degree=1 IsPeriodic=0
    g2: BSplineCurve PolesCount=2 KnotsCount=2 Degree=1 IsPeriodic=0
    g3: BSplineCurve PolesCount=2 KnotsCount=2 Degree=1 IsPeriodic=0
    g4: BSplineCurve PolesCount=2 KnotsCount=2 Degree=1 IsPeriodic=0
    g5: BSplineCurve PolesCount=2 KnotsCount=2 Degree=1 IsPeriodic=0
    g6: BSplineCurve PolesCount=2 KnotsCount=2 Degree=1 IsPeriodic=0
    g7: BSplineCurve PolesCount=2 KnotsCount=2 Degree=1 IsPeriodic=0
    g8: BSplineCurve PolesCount=2 KnotsCount=2 Degree=1 IsPeriodic=0
    g9: BSplineCurve PolesCount=2 KnotsCount=2 Degree=1 IsPeriodic=0
    g10: BSplineCurve PolesCount=2 KnotsCount=2 Degree=1 IsPeriodic=0
    g11: BSplineCurve PolesCount=2 KnotsCount=2 Degree=1 IsPeriodic=0
    g12: BSplineCurve PolesCount=2 KnotsCount=2 Degree=1 IsPeriodic=0
    g13: BSplineCurve PolesCount=2 KnotsCount=2 Degree=1 IsPeriodic=0
    g14: BSplineCurve PolesCount=2 KnotsCount=2 Degree=1 IsPeriodic=0
    g15: BSplineCurve PolesCount=2 KnotsCount=2 Degree=1 IsPeriodic=0
    g16: BSplineCurve PolesCount=2 KnotsCount=2 Degree=1 IsPeriodic=0
    g17: BSplineCurve PolesCount=2 KnotsCount=2 Degree=1 IsPeriodic=0
    g18: BSplineCurve PolesCount=2 KnotsCount=2 Degree=1 IsPeriodic=0
    g19: BSplineCurve PolesCount=2 KnotsCount=2 Degree=1 IsPeriodic=0
    g20: BSplineCurve PolesCount=2 KnotsCount=2 Degree=1 IsPeriodic=0
    g21: BSplineCurve PolesCount=2 KnotsCount=2 Degree=1 IsPeriodic=0
    g22: BSplineCurve PolesCount=2 KnotsCount=2 Degree=1 IsPeriodic=0
    g23: BSplineCurve PolesCount=2 KnotsCount=2 Degree=1 IsPeriodic=0
    g24: BSplineCurve PolesCount=2 KnotsCount=2 Degree=1 IsPeriodic=0
    g25: BSplineCurve PolesCount=2 KnotsCount=2 Degree=1 IsPeriodic=0
    g26: BSplineCurve PolesCount=2 KnotsCount=2 Degree=1 IsPeriodic=0
    g27: BSplineCurve PolesCount=2 KnotsCount=2 Degree=1 IsPeriodic=0
    g28: BSplineCurve PolesCount=2 KnotsCount=2 Degree=1 IsPeriodic=0
    g29: BSplineCurve PolesCount=2 KnotsCount=2 Degree=1 IsPeriodic=0
    g30: BSplineCurve PolesCount=2 KnotsCount=2 Degree=1 IsPeriodic=0
    g31: BSplineCurve PolesCount=2 KnotsCount=2 Degree=1 IsPeriodic=0
    g32: BSplineCurve PolesCount=2 KnotsCount=2 Degree=1 IsPeriodic=0
    g33: BSplineCurve PolesCount=2 KnotsCount=2 Degree=1 IsPeriodic=0
    g34: BSplineCurve PolesCount=2 KnotsCount=2 Degree=1 IsPeriodic=0
    g35: BSplineCurve PolesCount=2 KnotsCount=2 Degree=1 IsPeriodic=0
    g36: BSplineCurve PolesCount=2 KnotsCount=2 Degree=1 IsPeriodic=0
    g37: BSplineCurve PolesCount=2 KnotsCount=2 Degree=1 IsPeriodic=0
    g38: BSplineCurve PolesCount=2 KnotsCount=2 Degree=1 IsPeriodic=0
    g39: BSplineCurve PolesCount=2 KnotsCount=2 Degree=1 IsPeriodic=0
    g40: BSplineCurve PolesCount=2 KnotsCount=2 Degree=1 IsPeriodic=0
    g41: BSplineCurve PolesCount=2 KnotsCount=2 Degree=1 IsPeriodic=0
    g42: BSplineCurve PolesCount=2 KnotsCount=2 Degree=1 IsPeriodic=0
    g43: BSplineCurve PolesCount=2 KnotsCount=2 Degree=1 IsPeriodic=0
    g44: BSplineCurve PolesCount=2 KnotsCount=2 Degree=1 IsPeriodic=0
    g45: BSplineCurve PolesCount=2 KnotsCount=2 Degree=1 IsPeriodic=0
    g46: BSplineCurve PolesCount=2 KnotsCount=2 Degree=1 IsPeriodic=0
    g47: BSplineCurve PolesCount=2 KnotsCount=2 Degree=1 IsPeriodic=0
    g48: BSplineCurve PolesCount=2 KnotsCount=2 Degree=1 IsPeriodic=0
    g49: BSplineCurve PolesCount=2 KnotsCount=2 Degree=1 IsPeriodic=0
    g50: BSplineCurve PolesCount=2 KnotsCount=2 Degree=1 IsPeriodic=0
    g51: BSplineCurve PolesCount=2 KnotsCount=2 Degree=1 IsPeriodic=0
    g52: BSplineCurve PolesCount=2 KnotsCount=2 Degree=1 IsPeriodic=0
    g53: BSplineCurve PolesCount=2 KnotsCount=2 Degree=1 IsPeriodic=0
    g54: BSplineCurve PolesCount=2 KnotsCount=2 Degree=1 IsPeriodic=0
    g55: BSplineCurve PolesCount=2 KnotsCount=2 Degree=1 IsPeriodic=0
    g56: BSplineCurve PolesCount=2 KnotsCount=2 Degree=1 IsPeriodic=0
    g57: BSplineCurve PolesCount=2 KnotsCount=2 Degree=1 IsPeriodic=0
  constraints (55):
    c: Coincident(g2,g3)
    c: Coincident(g3,g4)
    c: Coincident(g4,g5)
    c: Coincident(g5,g6)
    c: Coincident(g6,g7)
    c: Coincident(g7,g8)
    c: Coincident(g8,g9)
    c: Coincident(g9,g10)
    c: Coincident(g10,g11)
    c: Coincident(g11,g12)
    c: Coincident(g12,g13)
    c: Coincident(g13,g14)
    c: Coincident(g14,g15)
    c: Coincident(g15,g16)
    c: Coincident(g16,g17)
    c: Coincident(g17,g18)
    c: Coincident(g18,g19)
    c: Coincident(g19,g20)
    c: Coincident(g20,g21)
    c: Coincident(g21,g22)
    c: Coincident(g22,g23)
    c: Coincident(g23,g24)
    c: Coincident(g24,g25)
    c: Coincident(g25,g26)
    c: Coincident(g26,g27)
    c: Coincident(g27,g28)
    c: Coincident(g28,g29)
    c: Coincident(g29,g30)
    c: Coincident(g30,g31)
    c: Coincident(g31,g32)
    c: Coincident(g32,g33)
    c: Coincident(g33,g34)
    c: Coincident(g34,g35)
    c: Coincident(g35,g36)
    c: Coincident(g36,g37)
    c: Coincident(g37,g38)
    c: Coincident(g38,g39)
    c: Coincident(g39,g40)
    c: Coincident(g40,g41)
    c: Coincident(g41,g42)
    c: Coincident(g42,g43)
    c: Coincident(g43,g44)
    c: Coincident(g44,g45)
    c: Coincident(g45,g46)
    c: Coincident(g46,g47)
    c: Coincident(g47,g48)
    c: Coincident(g48,g49)
    c: Coincident(g49,g50)
    c: Coincident(g50,g51)
    c: Coincident(g51,g52)
    c: Coincident(g52,g53)
    c: Coincident(g53,g54)
    c: Coincident(g54,g55)
    c: Coincident(g55,g56)
    c: Coincident(g56,g57)
FEATURE [PartDesign::Pad] Pad
  Direction = (1,1,1)
  Length = 5
  Length2 = 100
  Profile = -> Sketch006
  Type = 0
FEATURE [PartDesign::Body] Body006  label="Part19"
  Group = -> [Sketch006,Pad]
  Origin = -> Origin006
  Tip = -> Pad
FEATURE [PartDesign::Pad] Pad001
  Direction = (1,1,1)
  Length = 5
  Length2 = 100
  Profile = -> Sketch005
  Type = 0
FEATURE [PartDesign::Body] Body005  label="Part18"
  Group = -> [Sketch005,Pad001]
  Origin = -> Origin005
  Tip = -> Pad001
FEATURE [PartDesign::Pad] Pad002
  Direction = (1,1,1)
  Length = 5
  Length2 = 100
  Profile = -> Sketch004
  Type = 0
FEATURE [PartDesign::Body] Body004  label="Part17"
  Group = -> [Sketch004,Pad002]
  Origin = -> Origin004
  Tip = -> Pad002
FEATURE [PartDesign::Pad] Pad003
  Direction = (1,1,1)
  Length = 5
  Length2 = 100
  Profile = -> Sketch003
  Type = 0
FEATURE [PartDesign::Body] Body003  label="Part16"
  Group = -> [Sketch003,Pad003]
  Origin = -> Origin003
  Tip = -> Pad003
FEATURE [PartDesign::Pad] Pad004
  Direction = (1,1,1)
  Length = 5
  Length2 = 100
  Profile = -> Sketch002
  Type = 0
FEATURE [PartDesign::Body] Body002  label="Part15"
  Group = -> [Sketch002,Pad004]
  Origin = -> Origin002
  Tip = -> Pad004
FEATURE [PartDesign::Pad] Pad005
  Direction = (1,1,1)
  Length = 5
  Length2 = 100
  Profile = -> Sketch001
  Type = 0
FEATURE [PartDesign::Body] Body001  label="Part14"
  Group = -> [Sketch001,Pad005]
  Origin = -> Origin001
  Tip = -> Pad005
FEATURE [PartDesign::Pad] Pad006
  Direction = (1,1,1)
  Length = 5
  Length2 = 100
  Profile = -> Sketch
  Type = 0
FEATURE [PartDesign::Body] Body  label="Part13"
  Group = -> [Sketch,Pad006]
  Origin = -> Origin
  Tip = -> Pad006
